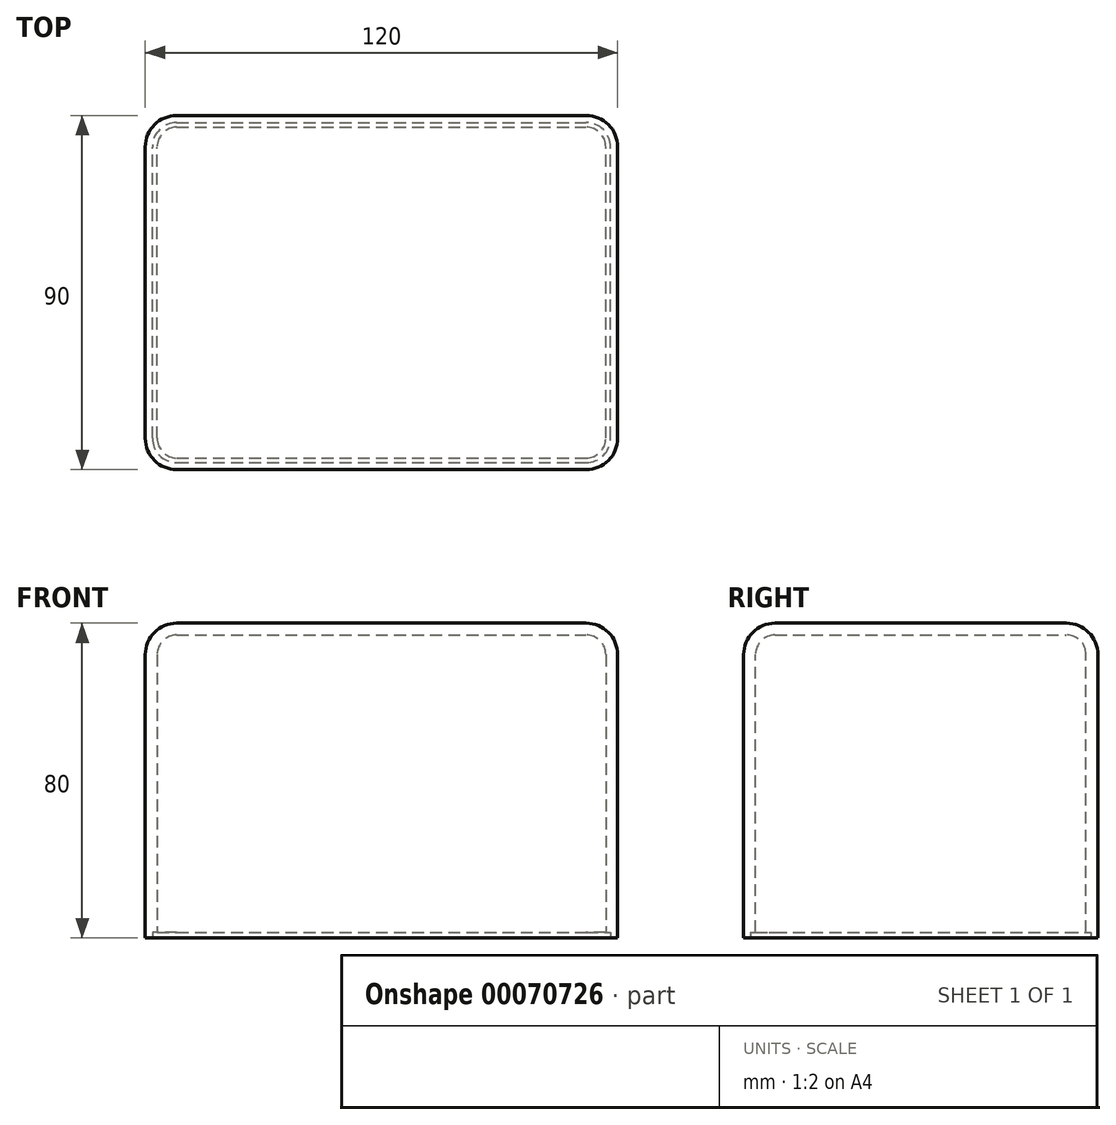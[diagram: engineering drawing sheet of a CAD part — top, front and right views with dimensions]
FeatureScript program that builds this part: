
annotation { "Feature Type Name" : "Feature", "Feature Type Description" : "" }
export const myFeature = defineFeature(function(context is Context, id is Id, definition is map)
    precondition{}
    {
        {
            var Q0;
            Q0=qCreatedBy(makeId("Front.planeOp"),FACE);
            var sketch = newSketch(context, id + "F0", { "sketchPlane" : qUnion([Q0])});
            skLineSegment(sketch, "E0.rect.bottom", {"start": v(-60, 40) * mm, "end": v(60, 40) * mm});
            skLineSegment(sketch, "E0.rect.top", {"start": v(-60, -40) * mm, "end": v(60, -40) * mm});
            skLineSegment(sketch, "E0.rect.left", {"start": v(-60, 40) * mm, "end": v(-60, -40) * mm});
            skLineSegment(sketch, "E0.rect.right", {"start": v(60, 40) * mm, "end": v(60, -40) * mm});
            skPoint(sketch, "E0.rect.middle", {"position": v(0, 0) * mm});
            skSolve(sketch);
        }
        {
            var Q0;
            Q0 = qSketchRegion(id + "F0", true);
            extrude(context, id + "F1", {"entities" : qUnion([Q0]), "depth" : 90 * mm, "symmetric" : true});
        }
        {
            var Q0;
            Q0=makeQuery(id+"F1.opExtrude","SWEPT_EDGE",EDGE,{"disambiguationData":[OSD([sQuery(id+"F0.wireOp",EDGE,"E0.rect.bottom"),sQuery(id+"F0.wireOp",EDGE,"E0.rect.right")])]});
            var Q1;
            Q1=makeQuery(id+"F1.opExtrude","CAP_EDGE",EDGE,{"disambiguationData":[OSD([sQuery(id+"F0.wireOp",EDGE,"E0.rect.right")])],"isStart":false});
            var Q2;
            Q2=makeQuery(id+"F1.opExtrude","CAP_EDGE",EDGE,{"disambiguationData":[OSD([sQuery(id+"F0.wireOp",EDGE,"E0.rect.right")])],"isStart":true});
            var Q3;
            Q3=makeQuery(id+"F1.opExtrude","CAP_EDGE",EDGE,{"disambiguationData":[OSD([sQuery(id+"F0.wireOp",EDGE,"E0.rect.left")])],"isStart":true});
            var Q4;
            Q4=makeQuery(id+"F1.opExtrude","CAP_EDGE",EDGE,{"disambiguationData":[OSD([sQuery(id+"F0.wireOp",EDGE,"E0.rect.bottom")])],"isStart":true});
            var Q5;
            Q5=makeQuery(id+"F1.opExtrude","SWEPT_EDGE",EDGE,{"disambiguationData":[OSD([sQuery(id+"F0.wireOp",EDGE,"E0.rect.bottom"),sQuery(id+"F0.wireOp",EDGE,"E0.rect.left")])]});
            var Q6;
            Q6=makeQuery(id+"F1.opExtrude","CAP_EDGE",EDGE,{"disambiguationData":[OSD([sQuery(id+"F0.wireOp",EDGE,"E0.rect.left")])],"isStart":false});
            var Q7;
            Q7=makeQuery(id+"F1.opExtrude","CAP_EDGE",EDGE,{"disambiguationData":[OSD([sQuery(id+"F0.wireOp",EDGE,"E0.rect.bottom")])],"isStart":false});
            fillet(context, id + "F2", {"entities" : qUnion([Q0, Q1, Q2, Q3, Q4, Q5, Q6, Q7]), "radius" : 8 * mm, "tangentPropagation" : true, "allowEdgeOverflow" : false});
        }
        {
            var Q0;
            Q0=makeQuery(id+"F1.opExtrude","SWEPT_FACE",FACE,{"disambiguationData":[OSD([sQuery(id+"F0.wireOp",EDGE,"E0.rect.top")])]});
            shell(context, id + "F3", {"entities" : qUnion([Q0]), "thickness" : 3 * mm});
        }
        {
            var Q0;
            Q0=makeQuery(id+"F1.opExtrude","SWEPT_FACE",FACE,{"disambiguationData":[OSD([sQuery(id+"F0.wireOp",EDGE,"E0.rect.top")])]});
            var sketch = newSketch(context, id + "F4", { "sketchPlane" : qUnion([Q0])});
            skLineSegment(sketch, "E1.0", {"start": v(-52, 43.2) * mm, "end": v(52, 43.2) * mm});
            skArc(sketch, "E1.1", {"start": v(58.2, 37) * mm, "mid": v(56.38, 41.38) * mm, "end": v(52, 43.2) * mm});
            skArc(sketch, "E1.2", {"start": v(-52, 43.2) * mm, "mid": v(-56.38, 41.38) * mm, "end": v(-58.2, 37) * mm});
            skLineSegment(sketch, "E1.3", {"start": v(58.2, 37) * mm, "end": v(58.2, -37) * mm});
            skLineSegment(sketch, "E1.4", {"start": v(-58.2, 37) * mm, "end": v(-58.2, -37) * mm});
            skArc(sketch, "E1.5", {"start": v(-58.2, -37) * mm, "mid": v(-56.38, -41.38) * mm, "end": v(-52, -43.2) * mm});
            skLineSegment(sketch, "E1.6", {"start": v(-52, -43.2) * mm, "end": v(52, -43.2) * mm});
            skArc(sketch, "E1.7", {"start": v(52, -43.2) * mm, "mid": v(56.38, -41.38) * mm, "end": v(58.2, -37) * mm});
            skSolve(sketch);
        }
        {
            var Q0;
            Q0 = qSketchRegion(id + "F4", true);
            extrude(context, id + "F5", {"entities" : qUnion([Q0]), "operationType" : NewBodyOperationType.REMOVE, "oppositeDirection" : true, "depth" : 1.5 * mm});
        }
    });
